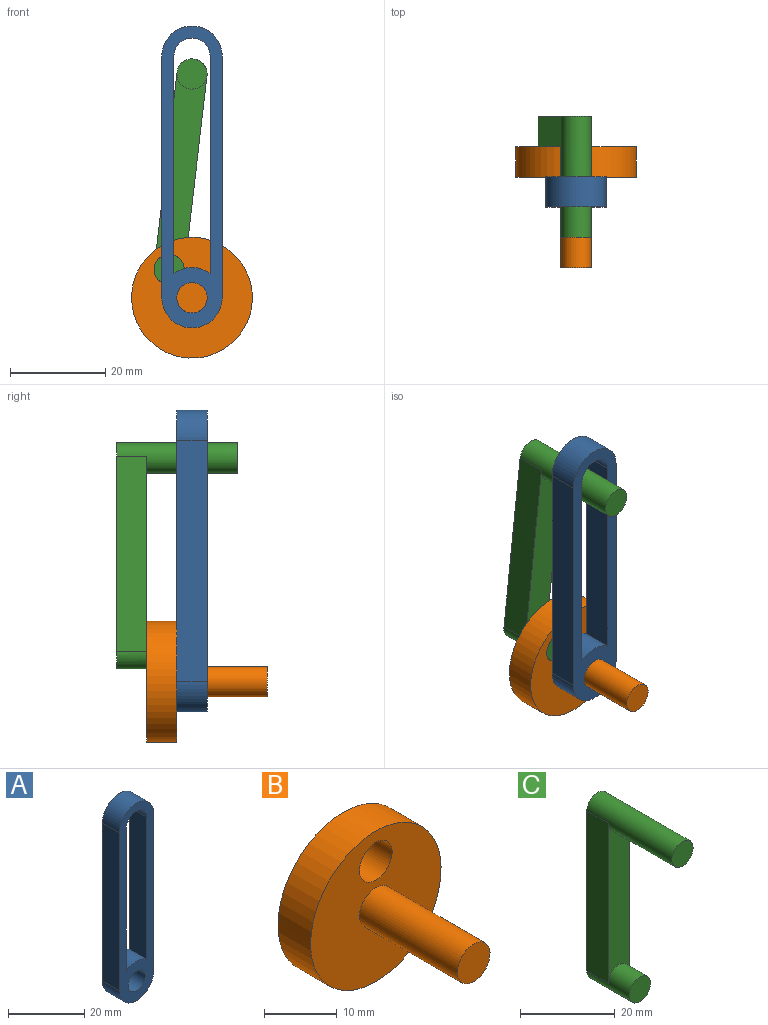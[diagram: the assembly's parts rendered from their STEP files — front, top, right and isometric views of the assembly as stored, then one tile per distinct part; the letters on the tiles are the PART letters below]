
ASSEMBLY  parts=3 mates=3
PART A: 11 faces, bbox 12.7x6.4x63.5 mm
  f0: cylinder r=6.35mm len=12.7mm, axis (0,1,0), area 126.7mm2, adj f1,f6,f9,f10
  f1: plane 50.8x6.35mm, normal (1,0,0), area 322.6mm2, adj f0,f2,f9,f10
  f2: cylinder r=6.35mm len=12.7mm, axis (0,1,0), area 126.7mm2, adj f1,f6,f9,f10
  f3: plane 45.72x6.35mm, normal (-1,0,0), area 290.3mm2, adj f4,f7,f9,f10
  f4: cylinder r=6.35mm len=7.62mm, axis (0,1,0), area 51.9mm2, adj f3,f5,f9,f10
  f5: plane 45.72x6.35mm, normal (1,0,0), area 290.3mm2, adj f4,f7,f9,f10
  f6: plane 50.8x6.35mm, normal (-1,0,0), area 322.6mm2, adj f0,f2,f9,f10
  f7: cylinder r=3.81mm len=7.62mm, axis (0,1,0), area 76mm2, adj f3,f5,f9,f10
  f8: cylinder r=3.17mm len=6.35mm, axis (0,1,0), area 126.7mm2, adj f9,f10
  f9: plane 63.5x12.7mm, normal (0,-1,0), area 375.6mm2, adj f0,f1,f2,f3,f4,f5,f6,f7
  f10: plane 63.5x12.7mm, normal (0,1,0), area 375.6mm2, adj f0,f1,f2,f3,f4,f5,f6,f7
PART B: 6 faces, bbox 25.4x25.4x25.4 mm
  f0: cylinder r=3.17mm len=6.35mm, axis (0,1,0), area 126.7mm2, adj f2,f3
  f1: cylinder r=12.7mm len=25.4mm, axis (0,1,0), area 506.7mm2, adj f2,f3
  f2: plane 25.4x25.4mm, normal (0,-1,0), area 443.4mm2, adj f0,f1,f4
  f3: plane 25.4x25.4mm, normal (0,1,0), area 475mm2, adj f0,f1
  f4: cylinder r=3.17mm len=19.05mm, axis (0,1,0), area 380mm2, adj f2,f5
  f5: plane 6.35x6.35mm, normal (0,-1,0), area 31.7mm2, adj f4
PART C: 8 faces, bbox 6.4x25.4x47.8 mm
  f0: plane 41.4x6.35mm, normal (1,0,0), area 262.9mm2, adj f2,f3,f4,f6
  f1: plane 41.4x6.35mm, normal (-1,0,0), area 262.9mm2, adj f2,f3,f4,f6
  f2: plane 41.4x6.35mm, normal (0,-1,0), area 231.2mm2, adj f0,f1,f4,f6
  f3: plane 47.75x6.35mm, normal (0,1,0), area 294.6mm2, adj f0,f1,f4,f6
  f4: cylinder r=3.17mm len=12.7mm, axis (0,1,0), area 190mm2, adj f0,f1,f2,f3,f5
  f5: plane 6.35x6.35mm, normal (0,-1,0), area 31.7mm2, adj f4
  f6: cylinder r=3.17mm len=25.4mm, axis (0,1,0), area 443.4mm2, adj f0,f1,f2,f3,f7
  f7: plane 6.35x6.35mm, normal (0,-1,0), area 31.7mm2, adj f6
PLACE A t=(-6.15,-3.31,-20.06)mm fixed
PLACE B rot(axis=(0,-1,0),38.9deg) t=(-6.15,3.04,-20.06)mm
PLACE C rot(axis=(0,1,0),6.6deg) t=(-10.94,9.39,-14.13)mm
MATE pin_slot C.f6 <-> A.f2  axis (0,1,0) through (-6.15,-3.31,26.99)mm
MATE revolute C.f4 <-> B.f0  axis (0,1,0) through (-10.94,-3.31,-14.13)mm
MATE revolute B.f4 <-> A.f8  axis (0,1,0) through (-6.15,-3.31,-20.06)mm
